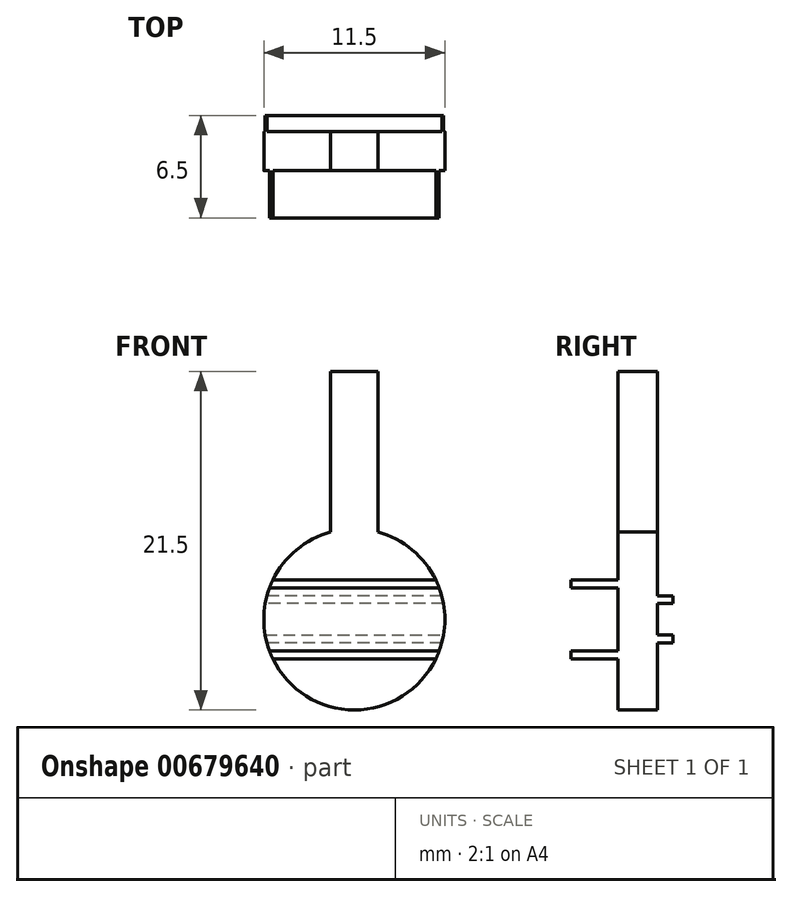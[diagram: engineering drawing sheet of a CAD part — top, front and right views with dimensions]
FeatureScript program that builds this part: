
annotation { "Feature Type Name" : "Feature", "Feature Type Description" : "" }
export const myFeature = defineFeature(function(context is Context, id is Id, definition is map)
    precondition{}
    {
        {
            var Q0;
            Q0=qCreatedBy(makeId("Front.planeOp"),FACE);
            var sketch = newSketch(context, id + "F0", { "sketchPlane" : qUnion([Q0])});
            skCircle(sketch, "E0", {"center": v(0, 0) * mm, "radius": 5.75 * mm});
            skLineSegment(sketch, "E1", {"start": v(-1.5, 5.75) * mm, "end": v(1.5, 5.75) * mm});
            skPoint(sketch, "E2", {"position": v(0, 5.75) * mm});
            skLineSegment(sketch, "E3", {"start": v(-1.5, 5.75) * mm, "end": v(-1.5, 5.55) * mm});
            skLineSegment(sketch, "E4", {"start": v(1.5, 5.75) * mm, "end": v(1.5, 5.55) * mm});
            skSolve(sketch);
        }
        {
            var Q0;
            Q0=makeQuery(id+"F0.imprint","IMPRINT",FACE,{"disambiguationData":[TD([[makeQuery(id+"F0.imprint","IMPRINT",EDGE,{"derivedFrom":sQuery(id+"F0.wireOp",EDGE,"E0")}),1.0]])]});
            extrude(context, id + "F1", {"entities" : qUnion([Q0]), "depth" : 2.5 * mm, "offsetDistance" : 25 * mm});
        }
        {
            var Q0;
            Q0=makeQuery(id+"F1.opExtrude","CAP_FACE",FACE,{"disambiguationData":[OSD([sQuery(id+"F0.wireOp",EDGE,"E0")])],"isStart":false});
            var sketch = newSketch(context, id + "F2", { "sketchPlane" : qUnion([Q0])});
            skLineSegment(sketch, "E5", {"start": v(-5.4, 2) * mm, "end": v(5.4, 2) * mm});
            skLineSegment(sketch, "E6", {"start": v(5.4, -2) * mm, "end": v(-5.4, -2) * mm});
            skLineSegment(sketch, "E7", {"start": v(-5.18, 2.5) * mm, "end": v(5.18, 2.5) * mm});
            skLineSegment(sketch, "E8", {"start": v(5.18, -2.5) * mm, "end": v(-5.18, -2.5) * mm});
            skLineSegment(sketch, "E9", {"start": v(-5.18, -2) * mm, "end": v(-5.18, -2.5) * mm});
            skLineSegment(sketch, "E10", {"start": v(5.18, -2) * mm, "end": v(5.18, -2.5) * mm});
            skLineSegment(sketch, "E11", {"start": v(-5.18, 2.5) * mm, "end": v(-5.18, 2) * mm});
            skLineSegment(sketch, "E12", {"start": v(5.18, 2.5) * mm, "end": v(5.18, 2) * mm});
            skSolve(sketch);
        }
        {
            var Q0;
            Q0 = qSketchRegion(id + "F2", true);
            var Q1;
            {var subQ3=sQuery(id+"F2.wireOp",EDGE,"E12");Q1=makeQuery(id+"F2.imprint","IMPRINT",FACE,{"disambiguationData":[TD([[makeQuery(id+"F2.imprint","IMPRINT",EDGE,{"derivedFrom":subQ3}),1.0]])]});}
            var Q2;
            {var subQ3=sQuery(id+"F2.wireOp",EDGE,"E11");Q2=makeQuery(id+"F2.imprint","IMPRINT",FACE,{"disambiguationData":[TD([[makeQuery(id+"F2.imprint","IMPRINT",EDGE,{"derivedFrom":subQ3}),-1.0]])]});}
            var Q3;
            {var subQ3=sQuery(id+"F2.wireOp",EDGE,"E9");Q3=makeQuery(id+"F2.imprint","IMPRINT",FACE,{"disambiguationData":[TD([[makeQuery(id+"F2.imprint","IMPRINT",EDGE,{"derivedFrom":subQ3}),-1.0]])]});}
            var Q4;
            {var subQ3=sQuery(id+"F2.wireOp",EDGE,"E10");Q4=makeQuery(id+"F2.imprint","IMPRINT",FACE,{"disambiguationData":[TD([[makeQuery(id+"F2.imprint","IMPRINT",EDGE,{"derivedFrom":subQ3}),1.0]])]});}
            extrude(context, id + "F3", {"entities" : qUnion([Q0, Q1, Q2, Q3, Q4]), "operationType" : NewBodyOperationType.ADD, "depth" : 3 * mm, "offsetDistance" : 25 * mm});
        }
        {
            var Q0;
            Q0=makeQuery(id+"F1.opExtrude","CAP_FACE",FACE,{"disambiguationData":[OSD([sQuery(id+"F0.wireOp",EDGE,"E0")])],"isStart":true});
            var sketch = newSketch(context, id + "F4", { "sketchPlane" : qUnion([Q0])});
            skLineSegment(sketch, "E13", {"start": v(-5.66, 1) * mm, "end": v(5.66, 1) * mm});
            skLineSegment(sketch, "E14", {"start": v(-5.55, 1.5) * mm, "end": v(5.55, 1.5) * mm});
            skLineSegment(sketch, "E15", {"start": v(5.66, -1) * mm, "end": v(-5.66, -1) * mm});
            skLineSegment(sketch, "E16", {"start": v(-5.55, -1.5) * mm, "end": v(5.55, -1.5) * mm});
            skLineSegment(sketch, "E17", {"start": v(5.55, 1.5) * mm, "end": v(5.55, 1) * mm});
            skLineSegment(sketch, "E18", {"start": v(5.55, -1) * mm, "end": v(5.55, -1.5) * mm});
            skLineSegment(sketch, "E19", {"start": v(-5.55, 1.5) * mm, "end": v(-5.55, 1) * mm});
            skLineSegment(sketch, "E20", {"start": v(-5.55, -1) * mm, "end": v(-5.55, -1.5) * mm});
            skSolve(sketch);
        }
        {
            var Q0;
            Q0 = qSketchRegion(id + "F4", true);
            var Q1;
            {var subQ3=sQuery(id+"F4.wireOp",EDGE,"E17");Q1=makeQuery(id+"F4.imprint","IMPRINT",FACE,{"disambiguationData":[TD([[makeQuery(id+"F4.imprint","IMPRINT",EDGE,{"derivedFrom":subQ3}),1.0]])]});}
            var Q2;
            {var subQ3=sQuery(id+"F4.wireOp",EDGE,"E18");Q2=makeQuery(id+"F4.imprint","IMPRINT",FACE,{"disambiguationData":[TD([[makeQuery(id+"F4.imprint","IMPRINT",EDGE,{"derivedFrom":subQ3}),1.0]])]});}
            var Q3;
            {var subQ3=sQuery(id+"F4.wireOp",EDGE,"E20");Q3=makeQuery(id+"F4.imprint","IMPRINT",FACE,{"disambiguationData":[TD([[makeQuery(id+"F4.imprint","IMPRINT",EDGE,{"derivedFrom":subQ3}),-1.0]])]});}
            var Q4;
            {var subQ3=sQuery(id+"F4.wireOp",EDGE,"E19");Q4=makeQuery(id+"F4.imprint","IMPRINT",FACE,{"disambiguationData":[TD([[makeQuery(id+"F4.imprint","IMPRINT",EDGE,{"derivedFrom":subQ3}),-1.0]])]});}
            extrude(context, id + "F5", {"entities" : qUnion([Q0, Q1, Q2, Q3, Q4]), "operationType" : NewBodyOperationType.ADD, "depth" : 1 * mm, "offsetDistance" : 25 * mm});
        }
        {
            var Q0;
            {var subQ0=sQuery(id+"F0.wireOp",EDGE,"E4");Q0=makeQuery(id+"F0.imprint","IMPRINT",FACE,{"disambiguationData":[TD([[makeQuery(id+"F0.imprint","IMPRINT",EDGE,{"derivedFrom":subQ0}),-1.0]])]});}
            var Q1;
            {var subQ0=sQuery(id+"F0.wireOp",EDGE,"E3");Q1=makeQuery(id+"F0.imprint","IMPRINT",FACE,{"disambiguationData":[TD([[makeQuery(id+"F0.imprint","IMPRINT",EDGE,{"derivedFrom":subQ0}),1.0]])]});}
            extrude(context, id + "F6", {"entities" : qUnion([Q0, Q1]), "operationType" : NewBodyOperationType.ADD, "depth" : 2.5 * mm, "offsetDistance" : 25 * mm});
        }
        {
            var Q0;
            {var subQ0=sQuery(id+"F0.wireOp",EDGE,"E1");Q0=makeQuery(id+"F6.boolean.opBoolean","MERGE",FACE,{"derivedFrom":[makeQuery(id+"F6.opExtrude","SWEPT_FACE",FACE,{"disambiguationData":[OSD([subQ0]),TDD([makeQuery(id+"F0.imprint","IMPRINT",EDGE,{"disambiguationData":[TD([[makeQuery(id+"F0.imprint","INTERSECT",VERTEX,{"derivedFrom":[subQ0,sQuery(id+"F0.wireOp",EDGE,"E3")]}),-1.0]])],"derivedFrom":subQ0})])]}),makeQuery(id+"F6.opExtrude","SWEPT_FACE",FACE,{"disambiguationData":[OSD([subQ0]),TDD([makeQuery(id+"F0.imprint","IMPRINT",EDGE,{"disambiguationData":[TD([[makeQuery(id+"F0.imprint","INTERSECT",VERTEX,{"derivedFrom":[subQ0,sQuery(id+"F0.wireOp",EDGE,"E4")]}),1.0]])],"derivedFrom":subQ0})])]})]});}
            var sketch = newSketch(context, id + "F7", { "sketchPlane" : qUnion([Q0])});
            skLineSegment(sketch, "E21.bottom", {"start": v(1.5, -2.5) * mm, "end": v(-1.5, -2.5) * mm});
            skLineSegment(sketch, "E21.top", {"start": v(1.5, 0) * mm, "end": v(-1.5, 0) * mm});
            skLineSegment(sketch, "E21.left", {"start": v(1.5, -2.5) * mm, "end": v(1.5, 0) * mm});
            skLineSegment(sketch, "E21.right", {"start": v(-1.5, -2.5) * mm, "end": v(-1.5, 0) * mm});
            skPoint(sketch, "E21.middle", {"position": v(0, -1.25) * mm});
            skPoint(sketch, "E21.middle.positionSnap0", {"position": v(-1.5, -1.25) * mm});
            skPoint(sketch, "E21.centerSnap0", {"position": v(-1.5, -1.25) * mm});
            skSolve(sketch);
        }
        {
            var Q0;
            Q0 = qSketchRegion(id + "F7", true);
            extrude(context, id + "F8", {"entities" : qUnion([Q0]), "operationType" : NewBodyOperationType.ADD, "depth" : 10 * mm, "offsetDistance" : 25 * mm});
        }
    });
